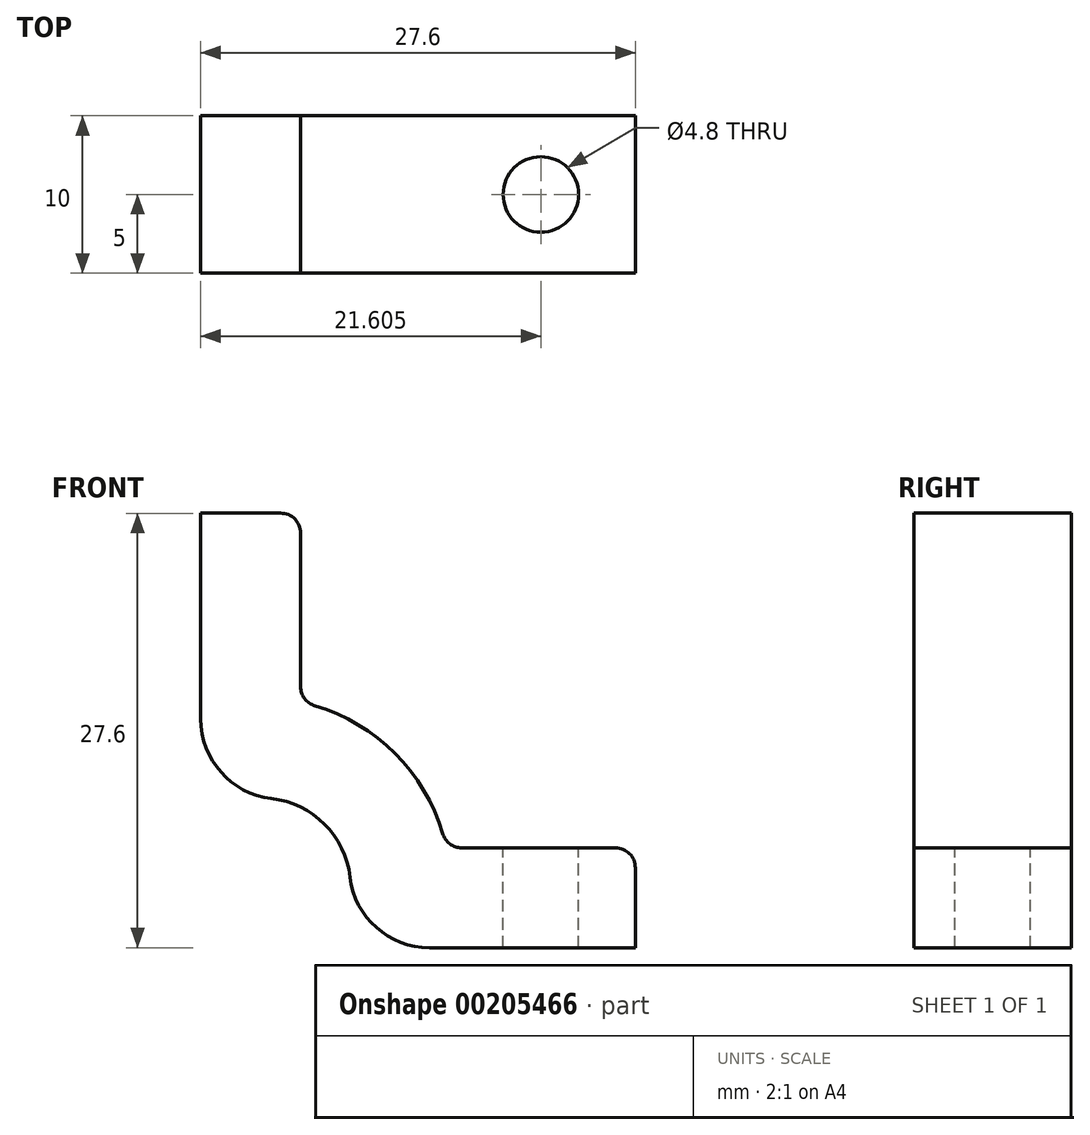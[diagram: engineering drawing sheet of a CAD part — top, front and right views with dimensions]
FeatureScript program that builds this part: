
annotation { "Feature Type Name" : "Feature", "Feature Type Description" : "" }
export const myFeature = defineFeature(function(context is Context, id is Id, definition is map)
    precondition{}
    {
        {
            var Q0;
            Q0=qCreatedBy(makeId("Front.planeOp"),FACE);
            var sketch = newSketch(context, id + "F0", { "sketchPlane" : qUnion([Q0])});
            skArc(sketch, "E0", {"start": v(5.72, 0) * mm, "mid": v(4.04, 4.04) * mm, "end": v(0, 5.72) * mm});
            skLineSegment(sketch, "E1", {"start": v(0, 0) * mm, "end": v(4.04, 4.04) * mm, "construction": true});
            skLineSegment(sketch, "E2", {"start": v(5.71, 0) * mm, "end": v(5.71, -3.81) * mm});
            skLineSegment(sketch, "E3", {"start": v(5.72, -3.81) * mm, "end": v(23.8, -3.8) * mm});
            skLineSegment(sketch, "E4", {"start": v(23.8, -3.8) * mm, "end": v(23.8, 2.54) * mm});
            skLineSegment(sketch, "E5", {"start": v(23.8, 2.54) * mm, "end": v(11.8, 2.54) * mm});
            skArc(sketch, "E6", {"start": v(11.8, 2.54) * mm, "mid": v(8.53, 8.53) * mm, "end": v(2.54, 11.8) * mm});
            skLineSegment(sketch, "E7.MirrorCS", {"start": v(-3.81, 23.8) * mm, "end": v(2.54, 23.8) * mm});
            skLineSegment(sketch, "E8.MirrorCS", {"start": v(-3.81, 5.71) * mm, "end": v(-3.81, 23.8) * mm});
            skLineSegment(sketch, "E9.MirrorCS", {"start": v(2.54, 23.8) * mm, "end": v(2.54, 11.8) * mm});
            skLineSegment(sketch, "E10.MirrorCS", {"start": v(0, 5.71) * mm, "end": v(-3.81, 5.71) * mm});
            skSolve(sketch);
        }
        {
            var Q0;
            Q0=makeQuery(id+"F0.imprint","IMPRINT",FACE,{"disambiguationData":[TD([[makeQuery(id+"F0.imprint","IMPRINT",EDGE,{"derivedFrom":sQuery(id+"F0.wireOp",EDGE,"E0")}),-1.0]])]});
            extrude(context, id + "F1", {"entities" : qUnion([Q0]), "depth" : 10 * mm});
        }
        {
            var Q0;
            Q0=makeQuery(id+"F1.opExtrude","SWEPT_FACE",FACE,{"disambiguationData":[OSD([sQuery(id+"F0.wireOp",EDGE,"E5")])]});
            var sketch = newSketch(context, id + "F2", { "sketchPlane" : qUnion([Q0])});
            skCircle(sketch, "E11", {"center": v(17.8, -5) * mm, "radius": 2.4 * mm});
            skSolve(sketch);
        }
        {
            var Q0;
            Q0=qSketchRegion(id+"F2",true);
            extrude(context, id + "F3", {"entities" : qUnion([Q0]), "operationType" : NewBodyOperationType.REMOVE, "endBound" : BoundingType.UP_TO_NEXT, "oppositeDirection" : true, "depth" : 25.4 * mm});
        }
        {
            var Q0;
            Q0=makeQuery(id+"F1.opExtrude","CAP_EDGE",EDGE,{"disambiguationData":[OSD([sQuery(id+"F0.wireOp",EDGE,"E0")])],"isStart":true});
            cPoint(context, id + "F4", {"entities" : qUnion([Q0]), "parameter" : 0.5});
        }
        {
            var Q0;
            Q0=makeQuery(id+"F1.opExtrude","CAP_EDGE",EDGE,{"disambiguationData":[OSD([sQuery(id+"F0.wireOp",EDGE,"E0")])],"isStart":false});
            cPoint(context, id + "F5", {"entities" : qUnion([Q0]), "parameter" : 0.5});
        }
        {
            var Q0;
            Q0=qCreatedBy(makeId("Origin.pointOp"),VERTEX);
            var Q1;
            Q1=qCreatedBy(id+"F4",VERTEX);
            var Q2;
            Q2=qCreatedBy(id+"F5",VERTEX);
            cPlane(context, id + "F6", {"entities" : qUnion([Q0, Q1, Q2]), "cplaneType" : CPlaneType.THREE_POINT, "offset" : 25.4 * mm, "width" : 152.4 * mm, "height" : 152.4 * mm});
        }
        {
            var Q0;
            Q0=makeQuery(id+"F1.opExtrude","SWEPT_EDGE",EDGE,{"disambiguationData":[OSD([sQuery(id+"F0.wireOp",EDGE,"E8.MirrorCS"),sQuery(id+"F0.wireOp",EDGE,"E10.MirrorCS")])]});
            var Q1;
            Q1=makeQuery(id+"F1.opExtrude","SWEPT_EDGE",EDGE,{"disambiguationData":[OSD([sQuery(id+"F0.wireOp",EDGE,"E2"),sQuery(id+"F0.wireOp",EDGE,"E3")])]});
            fillet(context, id + "F7", {"entities" : qUnion([Q0, Q1]), "radius" : 5.08 * mm, "tangentPropagation" : true, "allowEdgeOverflow" : false});
        }
        {
            var Q0;
            Q0=makeQuery(id+"F1.opExtrude","SWEPT_EDGE",EDGE,{"disambiguationData":[OSD([sQuery(id+"F0.wireOp",EDGE,"E9.MirrorCS"),sQuery(id+"F0.wireOp",EDGE,"3b9fe1af-a6ee-4d0d-95ef-19a645256aa44.MirrorCS")])]});
            var Q1;
            Q1=makeQuery(id+"F1.opExtrude","SWEPT_EDGE",EDGE,{"disambiguationData":[OSD([sQuery(id+"F0.wireOp",EDGE,"E5"),sQuery(id+"F0.wireOp",EDGE,"WnH2jzds-1Dp7-Dqyn-B2S7-A6DMInTQyFcN")])]});
            fillet(context, id + "F8", {"entities" : qUnion([Q0, Q1]), "radius" : 1.27 * mm, "tangentPropagation" : true, "allowEdgeOverflow" : false});
        }
    });
